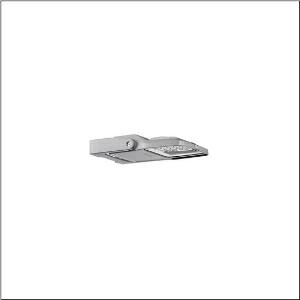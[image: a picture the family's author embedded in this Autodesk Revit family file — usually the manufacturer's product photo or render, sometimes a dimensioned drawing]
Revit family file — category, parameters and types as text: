
# Revit family: floodlight_fl_21_iq_micro___pl64_5xa7762a2e2a_90eb
name_source: partatom
category: Lighting Fixtures
units: mm (PartAtom-declared; Revit-internal decimal feet)

## family parameters
Cut with Voids When Loaded = No
Host = Face
Light Source = No
Part Type = Normal
Room Calculation Point = No
Round Connector Dimension = Use Diameter
Shared = No

## types (1)
- --- (1 x LED, 2870 lm, 23.1 W, 3000K)
    Apparent Load = 23 VA
    CIE Flux Codes = 28 80 98 100 100
    Color Rendering = 70
    Color Temperature = 3000K
    Default Elevation = 1800 mm
    Description = Floodlight FL 21 iQ micro, floodlight, primary light control with lens, of PMMA, primary optical cover: protective disc, of toughened safety glass, transparent, light distribution: PL64, light emission: direct distribution, installation type: surface-mounted, lamps: LED, High Power LED, rated values: 2.870lm | 23,1W | 124,2lm/W (begin service life); end service life: 2.870lm | 23,8W; at 50% lumin. flux: 1.435lm | 11W | 130,5lm/W, colour temperature: 3000K, colour rendering: CRI > 70, light colour: 730, light setting 1 begin service life: 100% | 2.870lm | 23,1W | 124,2lm/W | 3.000K, light setting 1 end service life: 23,8W, further light settings possible, control: Auto-Match, Temp-Guard, Night-Set, Smart-Wire, Desk-Remote (wireless, voltage-free reading and setting of iQ features in the workshop via application-optimized NFC function/RFID function), optimised constant luminous flux control (CLO 2.0), Street-Remote, pre-setting: linear dimming characteristic, with terminal, 6-pole, mains connection: 220..240V, AC, 50/60Hz, luminaire housing, of diecast aluminium, powder-coated, SITECO metallic grey (DB 702S), corrosivity category C5 mid according to DIN EN ISO 12944suitable for swimming poolschlorine-resistant, sealing non-destructively replaceable, design bracket, of diecast aluminium, powder-coated, SITECO metallic grey (DB 702S), protection rating (complete): IP66, insulation class (complete): insulation class II (safety insulation), certification: CE, ENEC, VDE, protection symbol: D, impact resistance: IK07, permissible operating ambient temperature: -40..+40°C, permissible operating ambient temperature for outdoor applications: -40..+50°C, standard: DIN EN 12944, LABS conformity tested according to VDMA 24364:2018-05, packaging unit: 1 piece

Light Distribution: PL64
    Height = 65 mm
    Lamp = 1 x LED
    Lamp Light Flux = 2870 lm
    Lamp Power = 23.1 W
    Lamp count = 1
    Length = 312 mm
    Luminous efficacy = 124 lm/W
    Manufacturer = Siteco
    ModVariant = No
    Model = 5XA7762A2E2A
    Mounting Place = Wall
    Mounting Type = Surface mounted
    Number of Poles = 1
    OnlyDefault = Yes
    Power Factor = 1
    Product Name = Floodlight FL 21 iQ micro | PL64
    Product group = floodlight | wall mounted
    ProductGroupID = 2002
    Protection Class = Protection class II
    Protection Degree = IP 66
    RLX_Detail_Level = 1
    RLX_Emergency_Light_Flux = 0 lm
    RLX_Emergency_Type = 0
    RLX_Emergency_Type_DB = No
    RlxData = <blob elided: 98481 chars, md5=fd790ecb>
    Socket = socket
    Standby Power = 0 W
    System Light Flux = 2870 lm
    System Power = 23 W
    Type Comments = factory setting: luminous flux: 100 % | dim-lin: 254 | 455 mA
    Type Image = l_1006878.jpg
    URL = http://relux.com
    VarID = @adj_180937
    Voltage = 0 V
    Weight = 0.00 kg
    Width = 230 mm

## geometry (parser evidence)
native form markers: Blend x4, Sweep x12
no freeform markers — native parametric forms only
